# Revit family: Bath-Drop_In-KOHLER-EVOK-K-1704T
name_source: partatom
category: Plumbing Fixtures
units: mm (PartAtom-declared; Revit-internal decimal feet)

## family parameters
Cut with Voids When Loaded = No
Host = Face
OmniClass Number = 23.31.15.00
OmniClass Title = Bathtubs
Part Type = Normal
Room Calculation Point = No
Round Connector Dimension = Use Diameter
Shared = No

## types (3) — shared parameters
ADA Compliant = No
Assembly Code = D2010500
CW Connection = No
Cold Water Inlet = Cold Water Inlet
Date Modified = 05/03/2024
Default Elevation = 0"
Finish = KOHLER-Acrylic-0-White
HW Connection = No
Hot Water Inlet = Hot Water Inlet
Length = 70 7/8"
Manufacturer = Kohler Co.
Master Format 2014 = 22 41 19
Master Format 2014 Name = Residential Bathtubs
Material = Acrylic
Product Name = EVOK
URL = http://www.kohler.com.cn
Vent Connection = No
Waste Connection = Yes
Waste Water Outlet = Waste Water Outlet
WaterSense Certified = No
Width = 31 1/2"

## per-type parameters (varying)
| type | Description | Drain Included | Model | Product Documentation Link | Product Page URL | Secondary Finish | Type |
| Orange Pillow, 0-White | Acrylic Bathtub (with pillow) | Yes | K-1704T-1P-0 | https://files.kohler.com.cn | https://www.kohler.com.cn | Kohler-Plastic-1P-Orange | 1 |
| Gray Pillow, 0-White | Acrylic Bathtub (with pillow) | Yes | K-1704T-58-0 | https://files.kohler.com.cn | https://www.kohler.com.cn | Kohler-Plastic-58-Thunder_Grey | 2 |
| Without Pillow, 0-White | Acrylic Bathtub, Without Pillow | No | K-1704T-Z-0 |  |  | KOHLER-Acrylic-0-White | 3 |

## geometry (parser evidence)
native form markers: Sweep x6
no freeform markers — native parametric forms only
